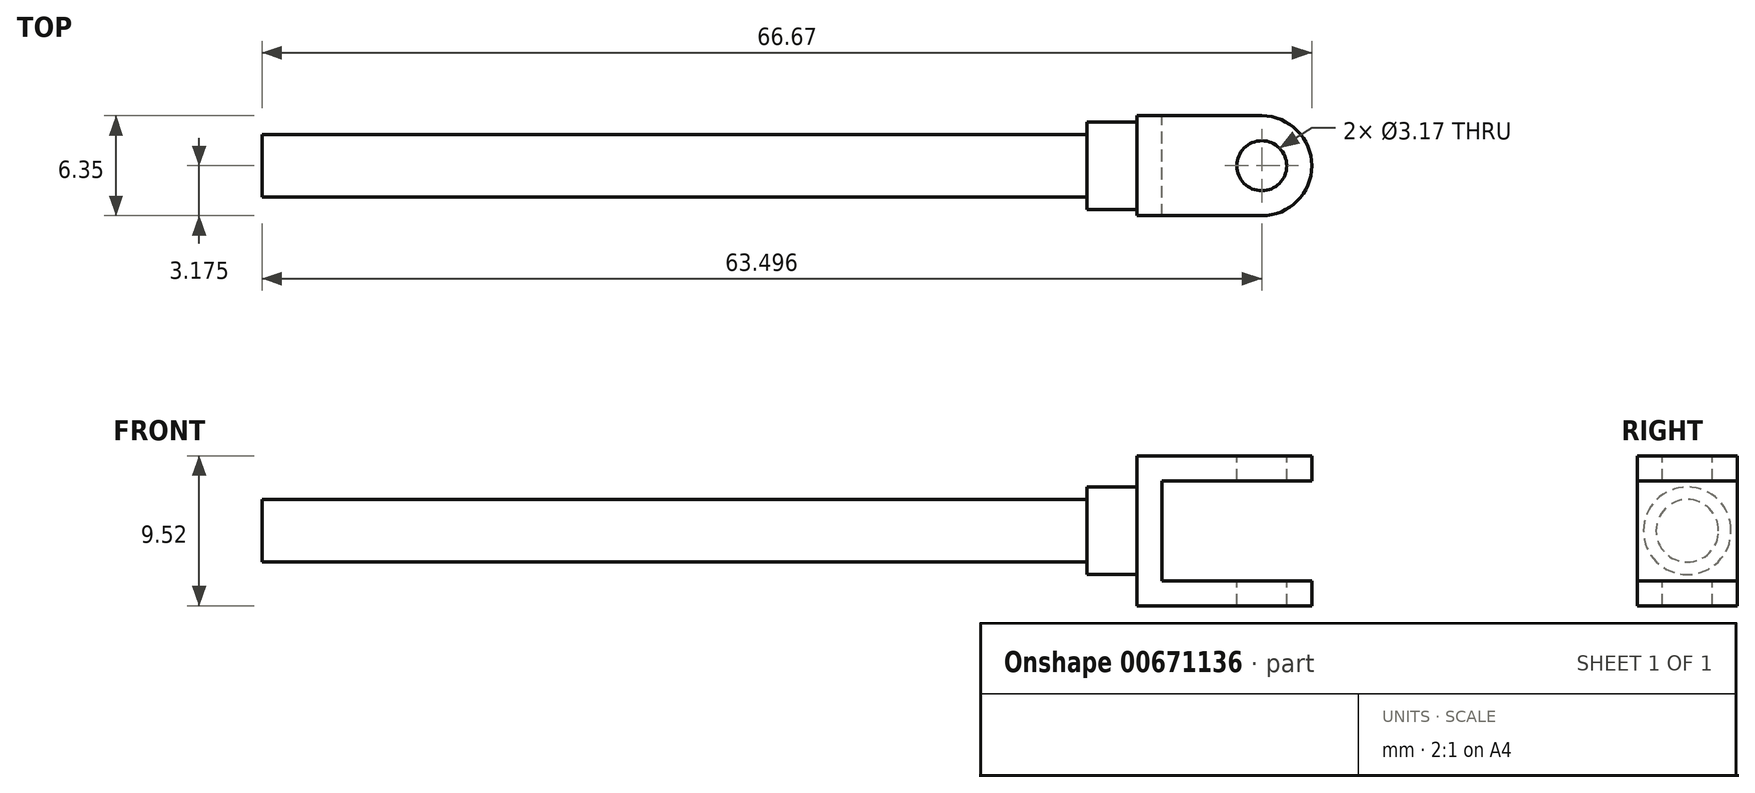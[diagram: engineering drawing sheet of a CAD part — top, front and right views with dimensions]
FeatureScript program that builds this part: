
annotation { "Feature Type Name" : "Feature", "Feature Type Description" : "" }
export const myFeature = defineFeature(function(context is Context, id is Id, definition is map)
    precondition{}
    {
        {
            var Q0;
            Q0=qCreatedBy(makeId("Front.planeOp"),FACE);
            var sketch = newSketch(context, id + "F0", { "sketchPlane" : qUnion([Q0])});
            skLineSegment(sketch, "E0", {"start": v(33.25, 28.06) * mm, "end": v(22.14, 28.06) * mm});
            skLineSegment(sketch, "E1", {"start": v(22.14, 28.06) * mm, "end": v(22.14, 18.54) * mm});
            skLineSegment(sketch, "E2", {"start": v(22.14, 18.54) * mm, "end": v(33.25, 18.54) * mm});
            skLineSegment(sketch, "E3", {"start": v(33.25, 18.54) * mm, "end": v(33.25, 20.12) * mm});
            skLineSegment(sketch, "E4", {"start": v(33.25, 20.12) * mm, "end": v(23.73, 20.12) * mm});
            skLineSegment(sketch, "E5", {"start": v(23.73, 20.12) * mm, "end": v(23.73, 26.47) * mm});
            skLineSegment(sketch, "E6", {"start": v(23.73, 26.47) * mm, "end": v(33.25, 26.47) * mm});
            skLineSegment(sketch, "E7", {"start": v(33.25, 26.47) * mm, "end": v(33.25, 28.06) * mm});
            skSolve(sketch);
        }
        {
            var Q0;
            Q0=qSketchRegion(id+"F0",true);
            extrude(context, id + "F1", {"entities" : qUnion([Q0]), "depth" : 6.35 * mm});
        }
        {
            var Q0;
            Q0=makeQuery(id+"F1.opExtrude","CAP_EDGE",EDGE,{"disambiguationData":[OSD([sQuery(id+"F0.wireOp",EDGE,"E3")])],"isStart":false});
            var Q1;
            Q1=makeQuery(id+"F1.opExtrude","CAP_EDGE",EDGE,{"disambiguationData":[OSD([sQuery(id+"F0.wireOp",EDGE,"E7")])],"isStart":false});
            var Q2;
            Q2=makeQuery(id+"F1.opExtrude","CAP_EDGE",EDGE,{"disambiguationData":[OSD([sQuery(id+"F0.wireOp",EDGE,"E7")])],"isStart":true});
            var Q3;
            Q3=makeQuery(id+"F1.opExtrude","CAP_EDGE",EDGE,{"disambiguationData":[OSD([sQuery(id+"F0.wireOp",EDGE,"E3")])],"isStart":true});
            fillet(context, id + "F2", {"entities" : qUnion([Q0, Q1, Q2, Q3]), "radius" : 3.17 * mm, "tangentPropagation" : true, "allowEdgeOverflow" : false});
        }
        {
            var Q0;
            Q0=makeQuery(id+"F1.opExtrude","SWEPT_FACE",FACE,{"disambiguationData":[OSD([sQuery(id+"F0.wireOp",EDGE,"E0")])]});
            var sketch = newSketch(context, id + "F3", { "sketchPlane" : qUnion([Q0])});
            skPoint(sketch, "E8", {"position": v(30.08, -3.18) * mm});
            skSolve(sketch);
        }
        {
            var Q0;
            Q0=sQuery(id+"F3.wireOp",VERTEX,"E8");
            var Q1;
            Q1=makeQuery(id+"F1.opExtrude","SWEPT_BODY",BODY,{"disambiguationData":[OSD([sQuery(id+"F0.wireOp",EDGE,"E0"),sQuery(id+"F0.wireOp",EDGE,"E1"),sQuery(id+"F0.wireOp",EDGE,"E2"),sQuery(id+"F0.wireOp",EDGE,"E3"),sQuery(id+"F0.wireOp",EDGE,"E4"),sQuery(id+"F0.wireOp",EDGE,"E5"),sQuery(id+"F0.wireOp",EDGE,"E6"),sQuery(id+"F0.wireOp",EDGE,"E7")])]});
            hole(context, id + "F4", {"style" : HoleStyle.SIMPLE, "endStyle" : HoleEndStyle.THROUGH, "holeDiameter" : 3.17 * mm, "tappedDepth" : 12.7 * mm, "tapClearance" : 3, "locations" : qUnion([Q0]), "scope" : qUnion([Q1])});
        }
        {
            var Q0;
            Q0=makeQuery(id+"F1.opExtrude","SWEPT_FACE",FACE,{"disambiguationData":[OSD([sQuery(id+"F0.wireOp",EDGE,"E1")])]});
            var sketch = newSketch(context, id + "F5", { "sketchPlane" : qUnion([Q0])});
            skCircle(sketch, "E9", {"center": v(3.18, 23.3) * mm, "radius": 2.78 * mm});
            skSolve(sketch);
        }
        {
            var Q0;
            Q0=qSketchRegion(id+"F5",true);
            extrude(context, id + "F6", {"entities" : qUnion([Q0]), "operationType" : NewBodyOperationType.ADD, "depth" : 3.17 * mm});
        }
        {
            var Q0;
            Q0=makeQuery(id+"F6.opExtrude","CAP_FACE",FACE,{"disambiguationData":[OSD([sQuery(id+"F5.wireOp",EDGE,"E9")])],"isStart":false});
            var sketch = newSketch(context, id + "F7", { "sketchPlane" : qUnion([Q0])});
            skCircle(sketch, "E10", {"center": v(3.18, 23.3) * mm, "radius": 1.98 * mm});
            skSolve(sketch);
        }
        {
            var Q0;
            Q0=qSketchRegion(id+"F7",true);
            extrude(context, id + "F8", {"entities" : qUnion([Q0]), "operationType" : NewBodyOperationType.ADD, "depth" : 52.4 * mm});
        }
    });
